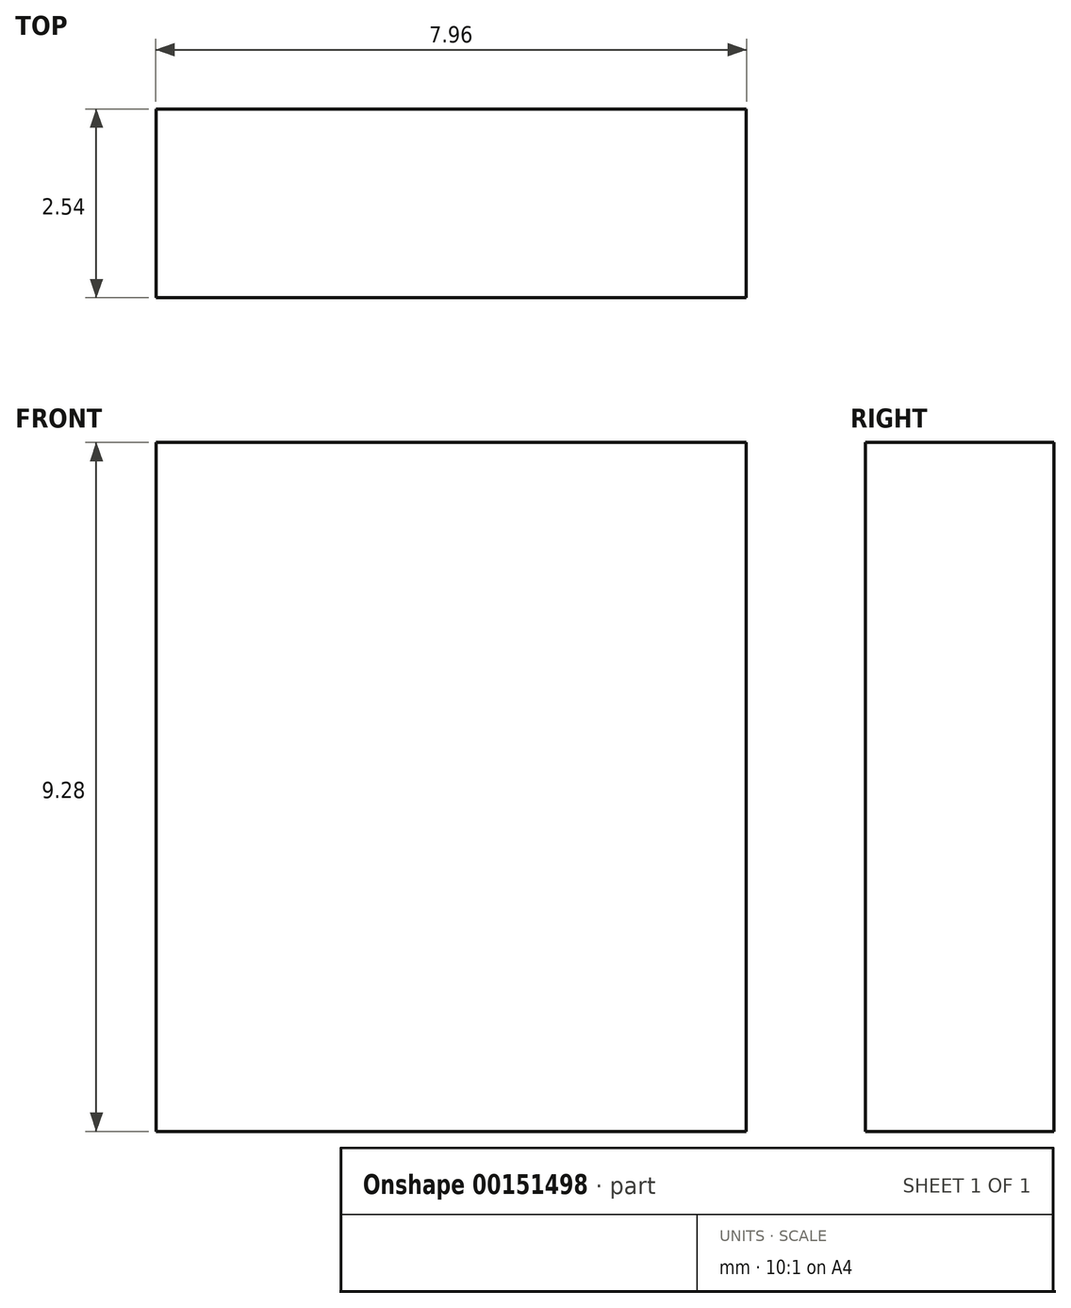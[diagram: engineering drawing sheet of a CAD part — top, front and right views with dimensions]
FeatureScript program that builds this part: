
annotation { "Feature Type Name" : "Feature", "Feature Type Description" : "" }
export const myFeature = defineFeature(function(context is Context, id is Id, definition is map)
    precondition{}
    {
        {
            var Q0;
            Q0=qCreatedBy(makeId("Front.planeOp"),FACE);
            var sketch = newSketch(context, id + "F0", { "sketchPlane" : qUnion([Q0])});
            skLineSegment(sketch, "E0.bottom", {"start": v(3.98, -4.64) * mm, "end": v(-3.98, -4.64) * mm});
            skLineSegment(sketch, "E0.top", {"start": v(3.98, 4.64) * mm, "end": v(-3.98, 4.64) * mm});
            skLineSegment(sketch, "E0.left", {"start": v(3.98, -4.64) * mm, "end": v(3.98, 4.64) * mm});
            skLineSegment(sketch, "E0.right", {"start": v(-3.98, -4.64) * mm, "end": v(-3.98, 4.64) * mm});
            skPoint(sketch, "E0.middle", {"position": v(0, 0) * mm});
            skSolve(sketch);
        }
        {
            var Q0;
            Q0=qCreatedBy(makeId("Front.planeOp"),FACE);
            var sketch = newSketch(context, id + "F1", { "sketchPlane" : qUnion([Q0])});
            skSolve(sketch);
        }
        {
            var Q0;
            Q0 = qSketchRegion(id + "F1", true);
            var Q1;
            Q1=makeQuery(id+"F0.imprint","IMPRINT",FACE,{"disambiguationData":[TD([[makeQuery(id+"F0.imprint","IMPRINT",EDGE,{"derivedFrom":sQuery(id+"F0.wireOp",EDGE,"E0.bottom")}),-1.0]])]});
            extrude(context, id + "F2", {"entities" : qUnion([Q0, Q1]), "depth" : 2.54 * mm});
        }
    });
